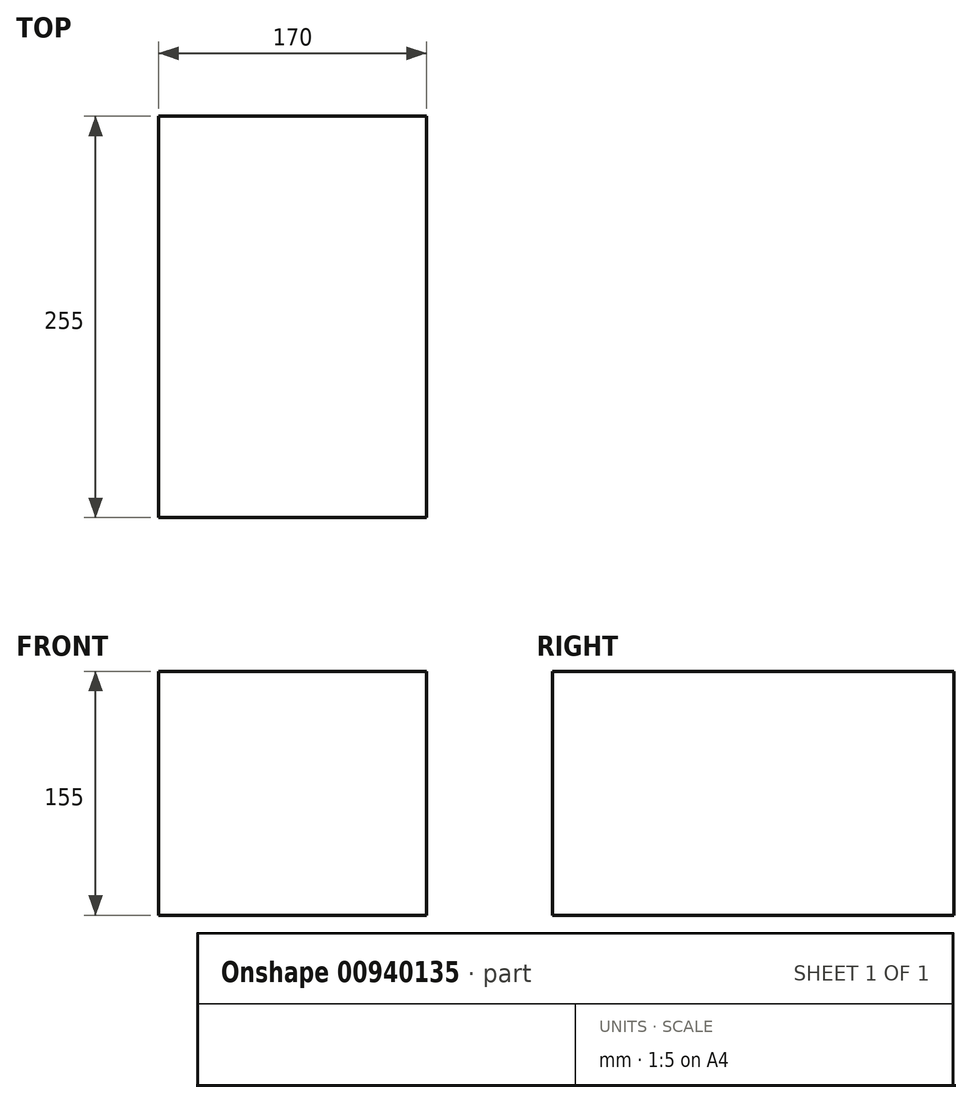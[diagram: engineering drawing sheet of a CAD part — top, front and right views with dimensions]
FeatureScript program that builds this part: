
annotation { "Feature Type Name" : "Feature", "Feature Type Description" : "" }
export const myFeature = defineFeature(function(context is Context, id is Id, definition is map)
    precondition{}
    {
        {
            var Q0;
            Q0=qCreatedBy(makeId("Right.planeOp"),FACE);
            var sketch = newSketch(context, id + "F0", { "sketchPlane" : qUnion([Q0])});
            skLineSegment(sketch, "E0.bottom", {"start": v(-128.09, 80.08) * mm, "end": v(126.91, 80.08) * mm});
            skLineSegment(sketch, "E0.top", {"start": v(-128.09, -74.92) * mm, "end": v(126.91, -74.92) * mm});
            skLineSegment(sketch, "E0.left", {"start": v(-128.09, 80.08) * mm, "end": v(-128.09, -74.92) * mm});
            skLineSegment(sketch, "E0.right", {"start": v(126.91, 80.08) * mm, "end": v(126.91, -74.92) * mm});
            skSolve(sketch);
        }
        {
            var Q0;
            Q0=makeQuery(id+"F0.imprint","IMPRINT",FACE,{"disambiguationData":[TD([[makeQuery(id+"F0.imprint","IMPRINT",EDGE,{"derivedFrom":sQuery(id+"F0.wireOp",EDGE,"E0.bottom")}),-1.0]])]});
            extrude(context, id + "F1", {"entities" : qUnion([Q0]), "depth" : 170 * mm, "offsetDistance" : 25 * mm});
        }
    });
